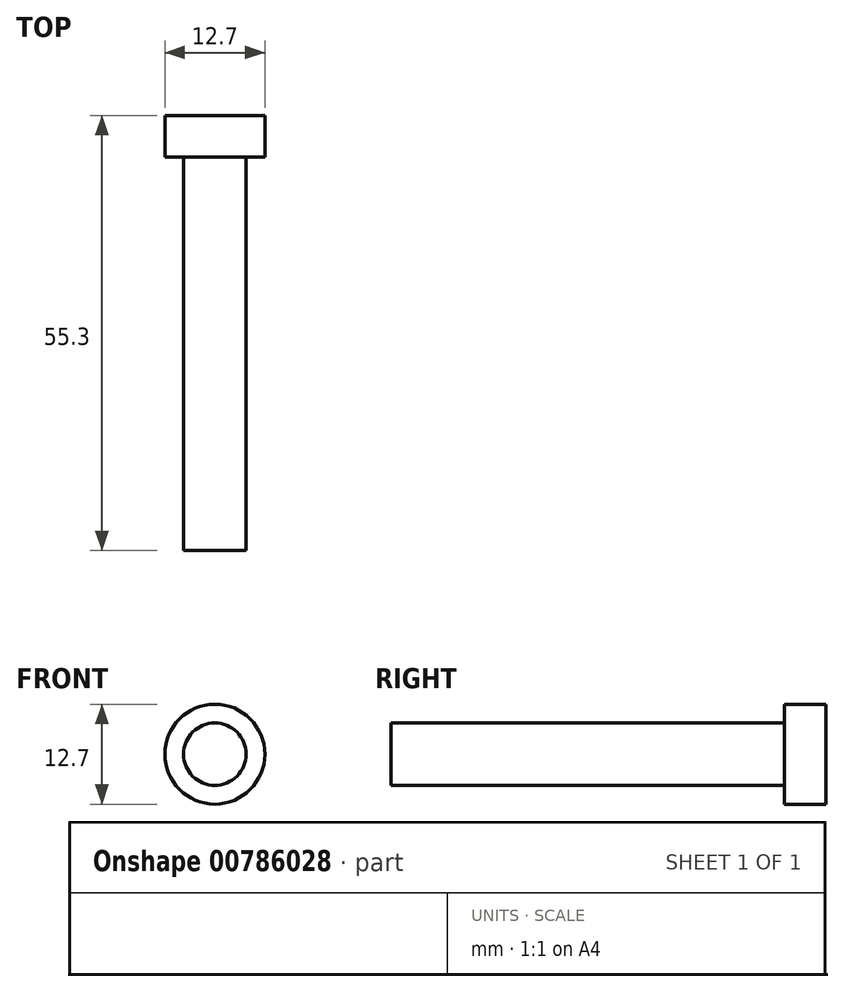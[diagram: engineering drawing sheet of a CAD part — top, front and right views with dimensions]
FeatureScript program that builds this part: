
annotation { "Feature Type Name" : "Feature", "Feature Type Description" : "" }
export const myFeature = defineFeature(function(context is Context, id is Id, definition is map)
    precondition{}
    {
        {
            assignVariable(context, id + "F0", {"name" : "boltHeadW", "anyValue" : 5.3 * mm});
        }
        {
            assignVariable(context, id + "F1", {"name" : "boltShankL", "anyValue" : 50 * mm});
        }
        {
            var Q0;
            Q0=qCreatedBy(makeId("Front.planeOp"),FACE);
            var sketch = newSketch(context, id + "F2", { "sketchPlane" : qUnion([Q0])});
            skCircle(sketch, "E0", {"center": v(0, 0) * mm, "radius": 6.35 * mm});
            skSolve(sketch);
        }
        {
            var Q0;
            Q0=qSketchRegion(id+"F2",true);
            extrude(context, id + "F3", {"entities" : qUnion([Q0]), "depth" : (getVariable(context, 'boltHeadW')), "offsetDistance" : 25 * mm});
        }
        {
            var Q0;
            Q0=makeQuery(id+"F3.opExtrude","CAP_FACE",FACE,{"disambiguationData":[OSD([sQuery(id+"F2.wireOp",EDGE,"E0")])],"isStart":false});
            var sketch = newSketch(context, id + "F4", { "sketchPlane" : qUnion([Q0])});
            skCircle(sketch, "E1", {"center": v(0, 0) * mm, "radius": 3.97 * mm});
            skSolve(sketch);
        }
        {
            var Q0;
            Q0=qSketchRegion(id+"F4",true);
            extrude(context, id + "F5", {"entities" : qUnion([Q0]), "operationType" : NewBodyOperationType.ADD, "depth" : getVariable(context, 'boltShankL'), "offsetDistance" : 25 * mm});
        }
    });
